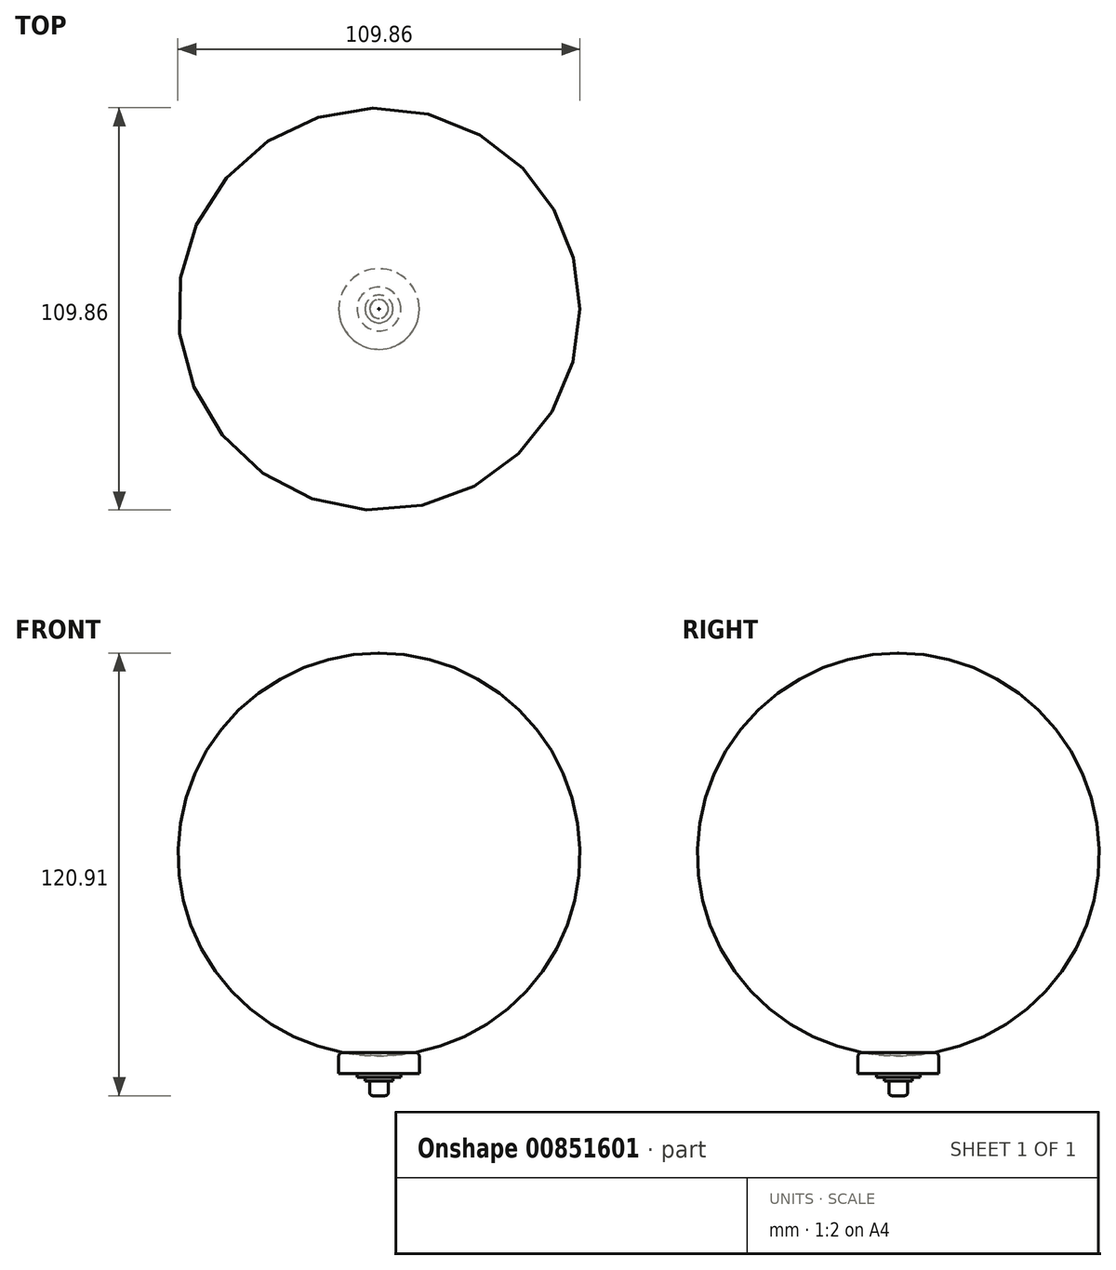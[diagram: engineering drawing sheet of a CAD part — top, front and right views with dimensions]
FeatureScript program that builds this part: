
annotation { "Feature Type Name" : "Feature", "Feature Type Description" : "" }
export const myFeature = defineFeature(function(context is Context, id is Id, definition is map)
    precondition{}
    {
        {
            var Q0;
            Q0=qCreatedBy(makeId("Front.planeOp"),FACE);
            var sketch = newSketch(context, id + "F0", { "sketchPlane" : qUnion([Q0])});
            skLineSegment(sketch, "E0", {"start": v(0, 18.8) * mm, "end": v(0, -20.61) * mm, "construction": true});
            skLineSegment(sketch, "E1", {"start": v(-2.55, -6.09) * mm, "end": v(-2.55, -0.09) * mm});
            skLineSegment(sketch, "E2", {"start": v(-2.55, -0.09) * mm, "end": v(-11, -0.09) * mm});
            skLineSegment(sketch, "E3", {"start": v(-11, -0.09) * mm, "end": v(-11, 5.91) * mm});
            skArc(sketch, "E4", {"start": v(-11, 5.91) * mm, "mid": v(-0.07, 4.82) * mm, "end": v(10.86, 5.91) * mm});
            skLineSegment(sketch, "E5", {"start": v(0, -6.09) * mm, "end": v(0, 4.82) * mm});
            skLineSegment(sketch, "E6", {"start": v(-2.55, -6.09) * mm, "end": v(0, -6.09) * mm});
            skLineSegment(sketch, "E7", {"start": v(-6, -0.09) * mm, "end": v(-6, -1.09) * mm});
            skLineSegment(sketch, "E8", {"start": v(-6, -1.09) * mm, "end": v(-2.55, -1.09) * mm});
            skSolve(sketch);
        }
        {
            var Q0;
            Q0=qSketchRegion(id+"F0",true);
            var Q1;
            Q1=sQuery(id+"F0.wireOp",EDGE,"E5");
            revolve(context, id + "F1", {"surfaceOperationType" : NewSurfaceOperationType.NEW, "entities" : qUnion([Q0]), "axis" : qUnion([Q1]), "revolveType" : RevolveType.FULL});
        }
        {
            var Q0;
            Q0=makeQuery(id+"F1.opRevolve","SWEPT_EDGE",EDGE,{"disambiguationData":[OSD([sQuery(id+"F0.wireOp",EDGE,"E3"),sQuery(id+"F0.wireOp",EDGE,"E4")])]});
            fillet(context, id + "F2", {"entities" : qUnion([Q0]), "radius" : 1 * mm, "tangentPropagation" : true, "allowEdgeOverflow" : false});
        }
        {
            var Q0;
            Q0=makeQuery(id+"F1.opRevolve","SWEPT_FACE",FACE,{"disambiguationData":[OSD([sQuery(id+"F0.wireOp",EDGE,"E6")])]});
            var sketch = newSketch(context, id + "F3", { "sketchPlane" : qUnion([Q0])});
            skCircle(sketch, "E9.0.0", {"center": v(0, 0) * mm, "radius": 2.55 * mm});
            skCircle(sketch, "E10.0", {"center": v(0, 0) * mm, "radius": 1.3 * mm});
            skSolve(sketch);
        }
        {
            var Q0;
            Q0=makeQuery(id+"F1.opRevolve","SWEPT_EDGE",EDGE,{"disambiguationData":[OSD([sQuery(id+"F0.wireOp",EDGE,"E1"),sQuery(id+"F0.wireOp",EDGE,"E6")])]});
            fillet(context, id + "F4", {"entities" : qUnion([Q0]), "radius" : 1 * mm, "tangentPropagation" : true, "rho" : 0.5, "crossSection" : FilletCrossSection.CONIC, "allowEdgeOverflow" : false});
        }
        {
            var Q0;
            Q0=makeQuery(id+"F1.opRevolve","SWEPT_FACE",FACE,{"disambiguationData":[OSD([sQuery(id+"F0.wireOp",EDGE,"E8")])]});
            var sketch = newSketch(context, id + "F5", { "sketchPlane" : qUnion([Q0])});
            skPoint(sketch, "E11.0", {"position": v(0, 0) * mm});
            skCircle(sketch, "E12", {"center": v(0, 0) * mm, "radius": 3.8 * mm});
            skSolve(sketch);
        }
        {
            var Q0;
            Q0 = qSketchRegion(id + "F5", true);
            extrude(context, id + "F6", {"entities" : qUnion([Q0]), "operationType" : NewBodyOperationType.ADD, "depth" : 1 * mm, "offsetDistance" : 25 * mm});
        }
    });
